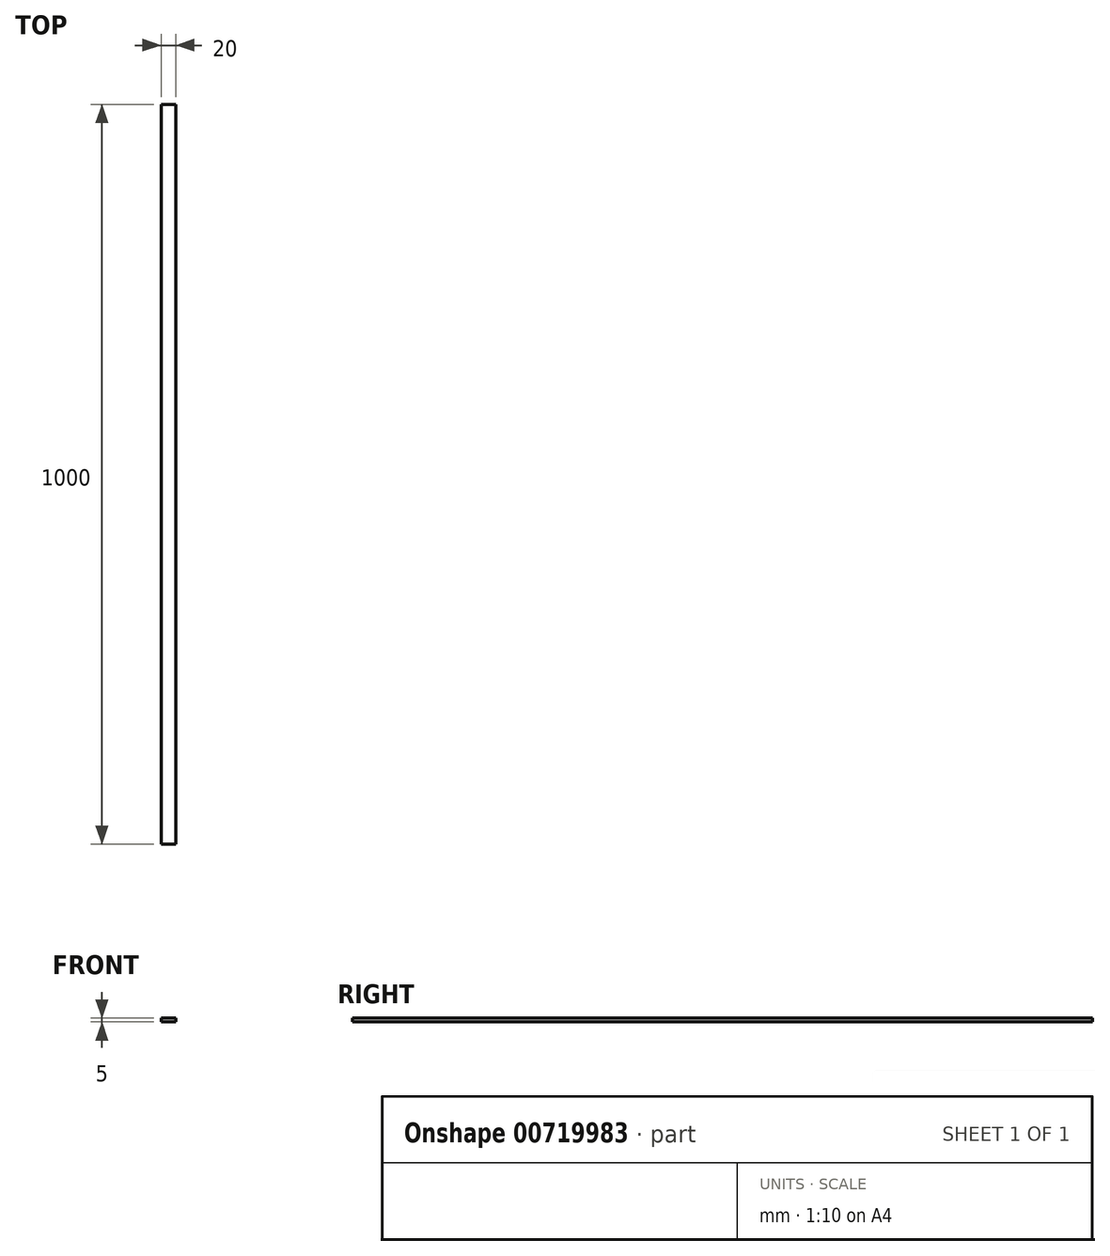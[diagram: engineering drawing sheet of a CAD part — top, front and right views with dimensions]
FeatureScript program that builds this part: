
annotation { "Feature Type Name" : "Feature", "Feature Type Description" : "" }
export const myFeature = defineFeature(function(context is Context, id is Id, definition is map)
    precondition{}
    {
        {
            var Q0;
            Q0=qCreatedBy(makeId("Front.planeOp"),FACE);
            var sketch = newSketch(context, id + "F0", { "sketchPlane" : qUnion([Q0])});
            skLineSegment(sketch, "E0.bottom", {"start": v(10, 2.5) * mm, "end": v(-10, 2.5) * mm});
            skLineSegment(sketch, "E0.top", {"start": v(10, -2.5) * mm, "end": v(-10, -2.5) * mm});
            skLineSegment(sketch, "E0.left", {"start": v(10, 2.5) * mm, "end": v(10, -2.5) * mm});
            skLineSegment(sketch, "E0.right", {"start": v(-10, 2.5) * mm, "end": v(-10, -2.5) * mm});
            skPoint(sketch, "E0.middle", {"position": v(0, 0) * mm});
            skSolve(sketch);
        }
        {
            var Q0;
            Q0=makeQuery(id+"F0.imprint","IMPRINT",FACE,{"disambiguationData":[TD([[makeQuery(id+"F0.imprint","IMPRINT",EDGE,{"derivedFrom":sQuery(id+"F0.wireOp",EDGE,"E0.bottom")}),1.0]])]});
            extrude(context, id + "F1", {"entities" : qUnion([Q0]), "depth" : 1000 * mm, "offsetDistance" : 25 * mm});
        }
    });
